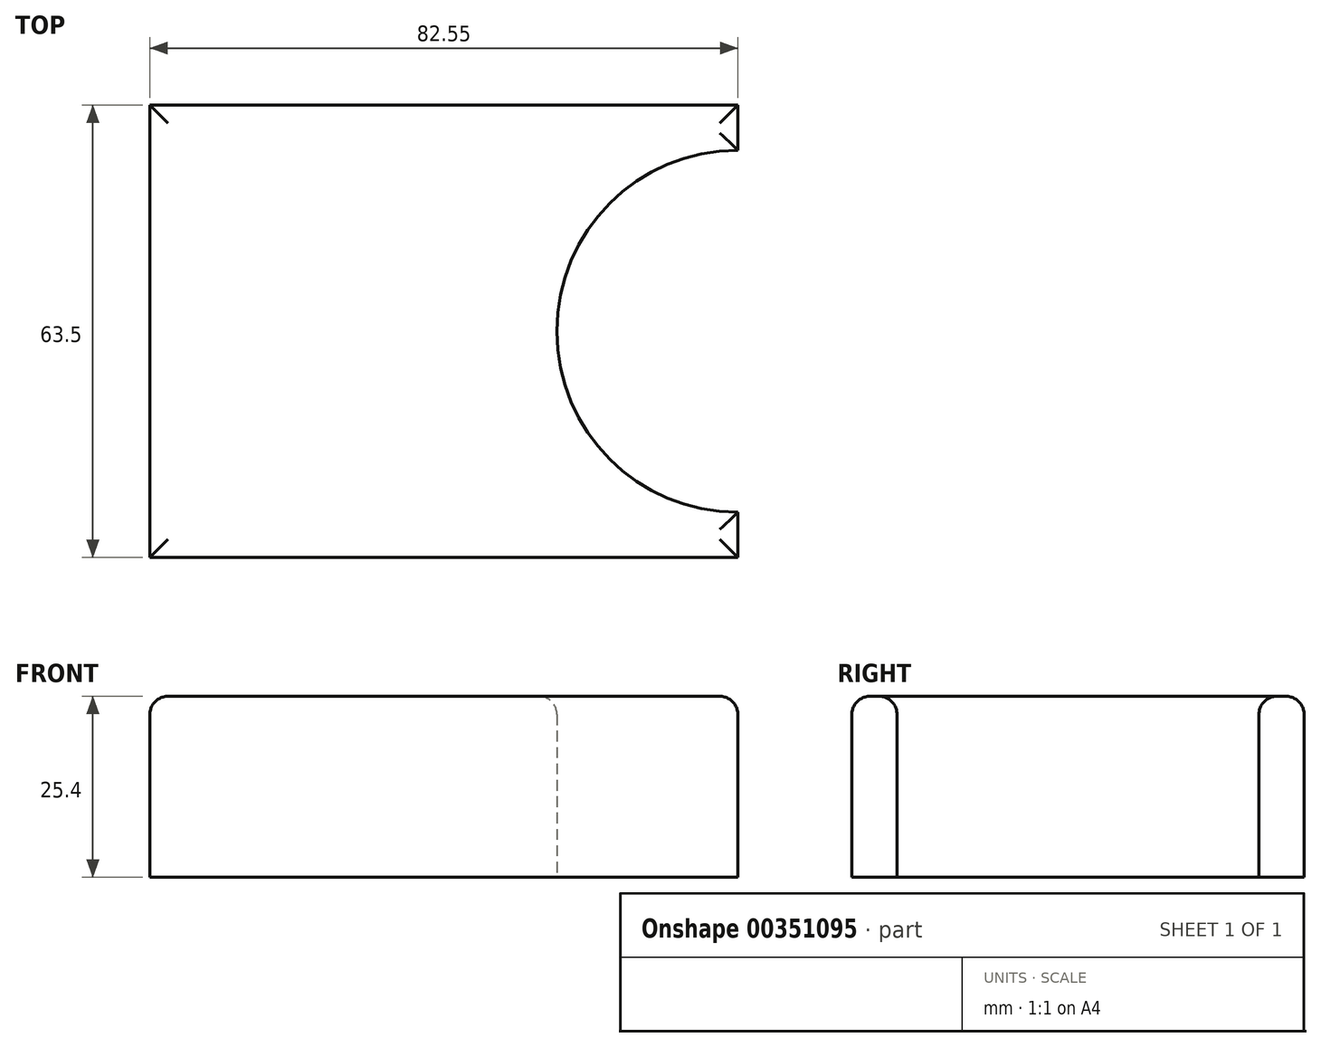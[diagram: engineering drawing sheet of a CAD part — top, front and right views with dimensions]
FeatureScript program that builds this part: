
annotation { "Feature Type Name" : "Feature", "Feature Type Description" : "" }
export const myFeature = defineFeature(function(context is Context, id is Id, definition is map)
    precondition{}
    {
        {
            var Q0;
            Q0=qCreatedBy(makeId("Top.planeOp"),FACE);
            var sketch = newSketch(context, id + "F0", { "sketchPlane" : qUnion([Q0])});
            skLineSegment(sketch, "E0.bottom", {"start": v(41.28, 31.75) * mm, "end": v(-41.27, 31.75) * mm});
            skLineSegment(sketch, "E0.top", {"start": v(41.27, -31.75) * mm, "end": v(-41.28, -31.75) * mm});
            skLineSegment(sketch, "E0.left", {"start": v(41.28, 31.75) * mm, "end": v(41.27, -31.75) * mm});
            skLineSegment(sketch, "E0.right", {"start": v(-41.27, 31.75) * mm, "end": v(-41.28, -31.75) * mm});
            skPoint(sketch, "E0.middle", {"position": v(0, 0) * mm});
            skCircle(sketch, "E1", {"center": v(41.28, 0) * mm, "radius": 25.4 * mm});
            skSolve(sketch);
        }
        {
            var Q0;
            {var subQ0=sQuery(id+"F0.wireOp",EDGE,"E1");var subQ1=sQuery(id+"F0.wireOp",EDGE,"E0.left");var subQ2=makeQuery(id+"F0.imprint","INTERSECT",VERTEX,{"disambiguationData":[OD(0.0)],"derivedFrom":[subQ1,subQ0]});Q0=makeQuery(id+"F0.imprint","IMPRINT",FACE,{"disambiguationData":[TD([[makeQuery(id+"F0.imprint","IMPRINT",EDGE,{"disambiguationData":[TD([[subQ2,-1.0]])],"derivedFrom":subQ1}),1.0]])]});}
            var Q1;
            {var subQ4=sQuery(id+"F0.wireOp",EDGE,"E0.bottom");Q1=makeQuery(id+"F0.imprint","IMPRINT",FACE,{"disambiguationData":[TD([[makeQuery(id+"F0.imprint","IMPRINT",EDGE,{"derivedFrom":subQ4}),1.0]])]});}
            var Q2;
            {var subQ0=sQuery(id+"F0.wireOp",EDGE,"E1");var subQ1=sQuery(id+"F0.wireOp",EDGE,"E0.left");var subQ2=makeQuery(id+"F0.imprint","INTERSECT",VERTEX,{"disambiguationData":[OD(0.0)],"derivedFrom":[subQ1,subQ0]});Q2=makeQuery(id+"F0.imprint","IMPRINT",FACE,{"disambiguationData":[TD([[makeQuery(id+"F0.imprint","IMPRINT",EDGE,{"disambiguationData":[TD([[subQ2,-1.0]])],"derivedFrom":subQ1}),-1.0]])]});}
            extrude(context, id + "F1", {"entities" : qUnion([Q0, Q1, Q2]), "depth" : 25.4 * mm});
        }
        {
            var Q0;
            Q0=makeQuery(id+"F1.opExtrude","CAP_EDGE",EDGE,{"disambiguationData":[OSD([sQuery(id+"F0.wireOp",EDGE,"E0.top")])],"isStart":false});
            var Q1;
            Q1=makeQuery(id+"F1.opExtrude","CAP_EDGE",EDGE,{"disambiguationData":[OSD([sQuery(id+"F0.wireOp",EDGE,"E0.right")])],"isStart":false});
            var Q2;
            Q2=makeQuery(id+"F1.opExtrude","CAP_EDGE",EDGE,{"disambiguationData":[OSD([sQuery(id+"F0.wireOp",EDGE,"E0.bottom")])],"isStart":false});
            var Q3;
            {var subQ0=sQuery(id+"F0.wireOp",EDGE,"E0.left");Q3=makeQuery(id+"F1.opExtrude","CAP_EDGE",EDGE,{"disambiguationData":[OSD([subQ0]),TDD([makeQuery(id+"F0.imprint","IMPRINT",EDGE,{"disambiguationData":[TD([[makeQuery(id+"F0.imprint","INTERSECT",VERTEX,{"derivedFrom":[sQuery(id+"F0.wireOp",EDGE,"E0.bottom"),subQ0]}),-1.0]])],"derivedFrom":subQ0})])],"isStart":false});}
            var Q4;
            Q4=makeQuery(id+"F1.opExtrude","CAP_EDGE",EDGE,{"disambiguationData":[OSD([sQuery(id+"F0.wireOp",EDGE,"E1")])],"isStart":false});
            var Q5;
            {var subQ0=sQuery(id+"F0.wireOp",EDGE,"E0.left");Q5=makeQuery(id+"F1.opExtrude","CAP_EDGE",EDGE,{"disambiguationData":[OSD([subQ0]),TDD([makeQuery(id+"F0.imprint","IMPRINT",EDGE,{"disambiguationData":[TD([[makeQuery(id+"F0.imprint","INTERSECT",VERTEX,{"derivedFrom":[sQuery(id+"F0.wireOp",EDGE,"E0.top"),subQ0]}),1.0]])],"derivedFrom":subQ0})])],"isStart":false});}
            fillet(context, id + "F2", {"entities" : qUnion([Q0, Q1, Q2, Q3, Q4, Q5]), "radius" : 2.54 * mm, "tangentPropagation" : true, "allowEdgeOverflow" : false});
        }
    });
